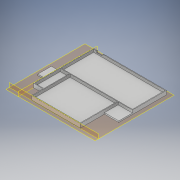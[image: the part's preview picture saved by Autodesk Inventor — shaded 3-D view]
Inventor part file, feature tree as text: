
AUTODESK INVENTOR PART (.ipt)
format: ipt  version: 2019 (Build 230136000, 136)  size: 186,880 bytes
history: native  units: mm
features: extrude x5, sketch x5, other x1, projected_geometry x1
ambient origin geometry x8: Origin, YZ Plane, XZ Plane, XY Plane, X Axis, Y Axis, Z Axis, Center Point
bodies: Body1 (feature_tree)
feature tree (12):
  other  "Těleso1"
  extrude  "Vysunutí1"  Depth=55.5mm
  extrude  "Vysunutí3"  TaperAngle=90.0deg  [1 undecoded]
  extrude  "Vysunutí4"  Depth=50.0mm
  extrude  "Vysunutí5"  Depth=107.0mm
  extrude  "Extrusion6"  Depth=1.8mm TaperAngle=0.0deg
  sketch  "Náčrt1"
  sketch  "Náčrt2"
  sketch  "Náčrt3"
  projected_geometry  "Promítnutá smyčka1"
  sketch  "Náčrt4"
  sketch  "Sketch5"  dims[d0=86.0mm d1=55.5mm d2=90.0deg d3=50.0mm d4=107.0mm d5=1.8mm d6=0.0mm d21=14.5mm d22=1.0mm d23=1.0mm d24=48.0mm d25=105.0mm d28=1.0mm d29=37.5mm d30=1.0mm d31=1.0mm d32=4.0mm d33=0.0mm d34=4.0mm d35=0.0mm d37=7.0mm d39=90.0deg d41=6.0mm d42=3.6mm d43=4.0mm d44=0.0mm d45=1.0mm d46=1.0mm d47=1.0mm d48=54.5mm d49=1.0mm d50=1.0mm d51=69.5mm d52=20.0mm d53=12.0mm d54=20.0mm d55=18.5mm d56=2.0mm d57=0.0mm]
note: 1 required parameter value undecoded (feature->parameter linkage not recoverable at this tier; creation-order binding heuristic only, values carry confidence <= 0.55)
